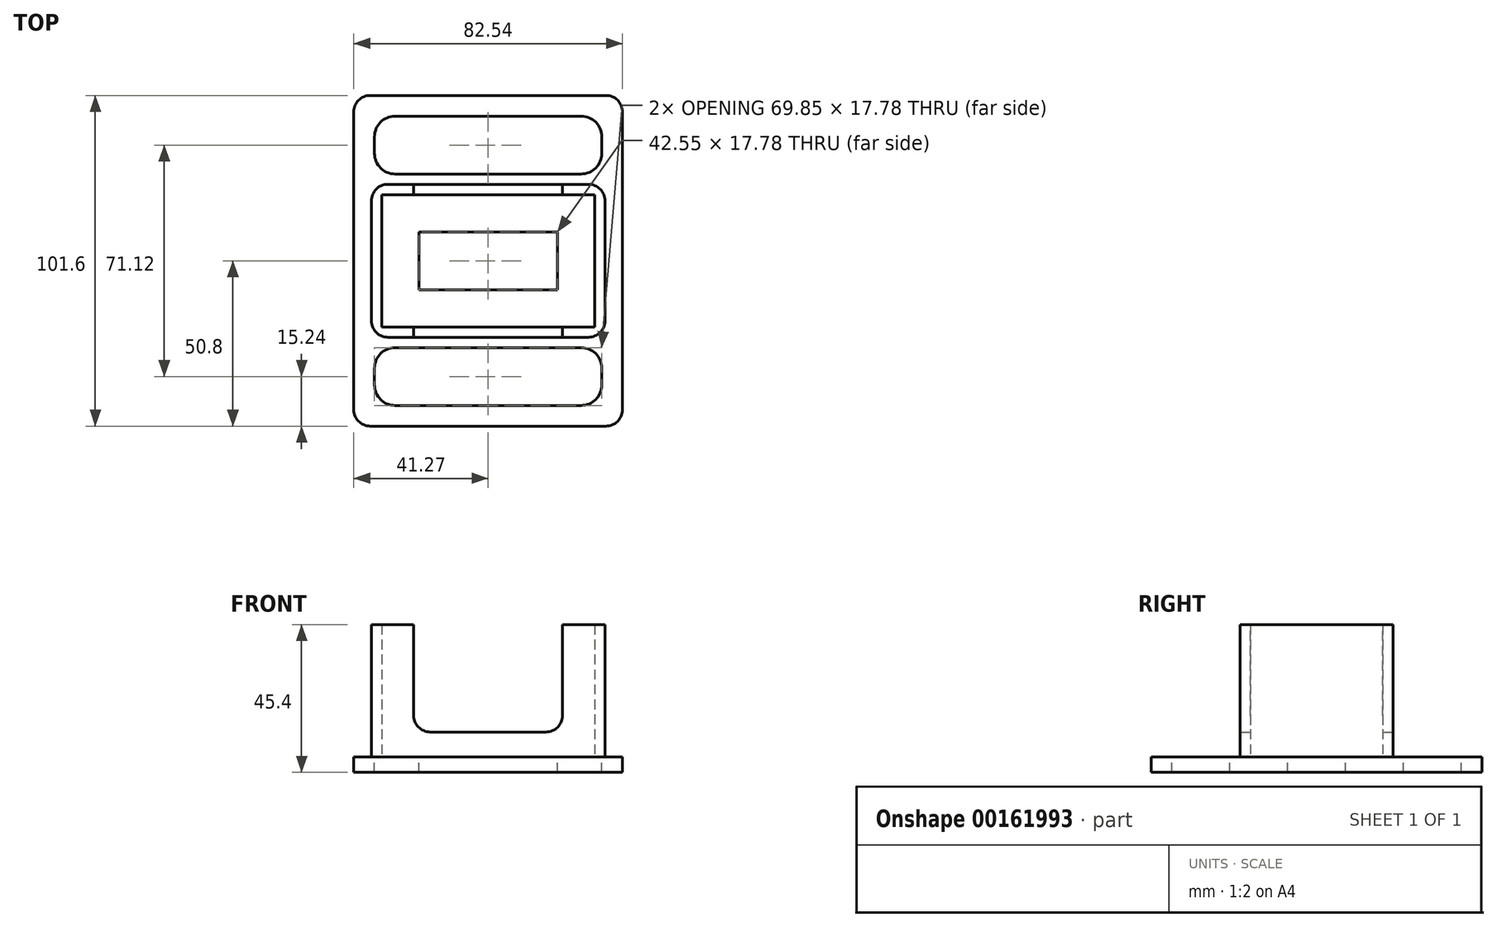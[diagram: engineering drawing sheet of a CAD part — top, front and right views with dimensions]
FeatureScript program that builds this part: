
annotation { "Feature Type Name" : "Feature", "Feature Type Description" : "" }
export const myFeature = defineFeature(function(context is Context, id is Id, definition is map)
    precondition{}
    {
        {
            var Q0;
            Q0=qCreatedBy(makeId("Top.planeOp"),FACE);
            var sketch = newSketch(context, id + "F0", { "sketchPlane" : qUnion([Q0])});
            skLineSegment(sketch, "E0.bottom", {"start": v(-41.27, 50.8) * mm, "end": v(41.28, 50.8) * mm});
            skLineSegment(sketch, "E0.top", {"start": v(-41.28, -50.8) * mm, "end": v(41.28, -50.8) * mm});
            skLineSegment(sketch, "E0.left", {"start": v(-41.27, 50.8) * mm, "end": v(-41.28, -50.8) * mm});
            skLineSegment(sketch, "E0.right", {"start": v(41.28, 50.8) * mm, "end": v(41.28, -50.8) * mm});
            skLineSegment(sketch, "E1", {"start": v(41.28, -50.8) * mm, "end": v(-41.27, 50.8) * mm, "construction": true});
            skSolve(sketch);
        }
        {
            var Q0;
            Q0 = qSketchRegion(id + "F0", true);
            extrude(context, id + "F1", {"entities" : qUnion([Q0]), "depth" : 4.76 * mm});
        }
        {
            var Q0;
            Q0=makeQuery(id+"F1.opExtrude","CAP_FACE",FACE,{"disambiguationData":[OSD([sQuery(id+"F0.wireOp",EDGE,"E0.bottom"),sQuery(id+"F0.wireOp",EDGE,"E0.top"),sQuery(id+"F0.wireOp",EDGE,"E0.left"),sQuery(id+"F0.wireOp",EDGE,"E0.right")])],"isStart":false});
            var sketch = newSketch(context, id + "F2", { "sketchPlane" : qUnion([Q0])});
            skLineSegment(sketch, "E2.bottom", {"start": v(-32.7, 20.32) * mm, "end": v(32.7, 20.32) * mm});
            skLineSegment(sketch, "E2.top", {"start": v(-32.7, -20.32) * mm, "end": v(32.7, -20.32) * mm});
            skLineSegment(sketch, "E2.left", {"start": v(-32.7, 20.32) * mm, "end": v(-32.7, -20.32) * mm});
            skLineSegment(sketch, "E2.right", {"start": v(32.7, 20.32) * mm, "end": v(32.7, -20.32) * mm});
            skPoint(sketch, "E2.middle", {"position": v(0, 0) * mm});
            skLineSegment(sketch, "E3.0", {"start": v(-35.88, 23.5) * mm, "end": v(35.88, 23.5) * mm});
            skLineSegment(sketch, "E3.1", {"start": v(-35.88, 23.5) * mm, "end": v(-35.88, -23.5) * mm});
            skLineSegment(sketch, "E3.2", {"start": v(-35.88, -23.5) * mm, "end": v(35.88, -23.5) * mm});
            skLineSegment(sketch, "E3.3", {"start": v(35.88, 23.5) * mm, "end": v(35.88, -23.5) * mm});
            skSolve(sketch);
        }
        {
            var Q0;
            Q0 = qSketchRegion(id + "F2", true);
            extrude(context, id + "F3", {"entities" : qUnion([Q0]), "operationType" : NewBodyOperationType.ADD, "depth" : 40.64 * mm});
        }
        {
            var Q0;
            Q0=qCreatedBy(makeId("Front.planeOp"),FACE);
            var sketch = newSketch(context, id + "F4", { "sketchPlane" : qUnion([Q0])});
            skLineSegment(sketch, "E4.bottom", {"start": v(22.86, 12.42) * mm, "end": v(-22.86, 12.42) * mm});
            skLineSegment(sketch, "E4.top", {"start": v(22.86, 45.4) * mm, "end": v(-22.86, 45.4) * mm});
            skLineSegment(sketch, "E4.left", {"start": v(22.86, 12.42) * mm, "end": v(22.86, 45.4) * mm});
            skLineSegment(sketch, "E4.right", {"start": v(-22.86, 12.42) * mm, "end": v(-22.86, 45.4) * mm});
            skPoint(sketch, "E4.middle", {"position": v(0, 28.91) * mm});
            skSolve(sketch);
        }
        {
            var Q0;
            Q0 = qSketchRegion(id + "F4", true);
            extrude(context, id + "F5", {"entities" : qUnion([Q0]), "operationType" : NewBodyOperationType.REMOVE, "endBound" : BoundingType.SYMMETRIC, "depth" : 80.26 * mm});
        }
        {
            var Q0;
            Q0=makeQuery(id+"F5.boolean.opBoolean","COPY",EDGE,{"derivedFrom":makeQuery(id+"F5.opExtrude","SWEPT_EDGE",EDGE,{"disambiguationData":[OSD([sQuery(id+"F4.wireOp",EDGE,"E4.bottom"),sQuery(id+"F4.wireOp",EDGE,"E4.right")])]})});
            var Q1;
            Q1=makeQuery(id+"F5.boolean.opBoolean","COPY",EDGE,{"derivedFrom":makeQuery(id+"F5.opExtrude","SWEPT_EDGE",EDGE,{"disambiguationData":[OSD([sQuery(id+"F4.wireOp",EDGE,"E4.bottom"),sQuery(id+"F4.wireOp",EDGE,"E4.left")])]})});
            fillet(context, id + "F6", {"entities" : qUnion([Q0, Q1]), "radius" : 5.08 * mm, "tangentPropagation" : true, "allowEdgeOverflow" : false});
        }
        {
            var Q0;
            Q0=makeQuery(id+"F3.opExtrude","SWEPT_EDGE",EDGE,{"disambiguationData":[OSD([sQuery(id+"F2.wireOp",EDGE,"E3.1"),sQuery(id+"F2.wireOp",EDGE,"E3.2")])]});
            var Q1;
            Q1=makeQuery(id+"F3.opExtrude","SWEPT_EDGE",EDGE,{"disambiguationData":[OSD([sQuery(id+"F2.wireOp",EDGE,"E3.0"),sQuery(id+"F2.wireOp",EDGE,"E3.1")])]});
            var Q2;
            Q2=makeQuery(id+"F3.opExtrude","SWEPT_EDGE",EDGE,{"disambiguationData":[OSD([sQuery(id+"F2.wireOp",EDGE,"E3.2"),sQuery(id+"F2.wireOp",EDGE,"E3.3")])]});
            var Q3;
            Q3=makeQuery(id+"F3.opExtrude","SWEPT_EDGE",EDGE,{"disambiguationData":[OSD([sQuery(id+"F2.wireOp",EDGE,"E3.0"),sQuery(id+"F2.wireOp",EDGE,"E3.3")])]});
            var Q4;
            Q4=makeQuery(id+"F1.opExtrude","SWEPT_EDGE",EDGE,{"disambiguationData":[OSD([sQuery(id+"F0.wireOp",EDGE,"E0.top"),sQuery(id+"F0.wireOp",EDGE,"E0.left")])]});
            var Q5;
            Q5=makeQuery(id+"F1.opExtrude","SWEPT_EDGE",EDGE,{"disambiguationData":[OSD([sQuery(id+"F0.wireOp",EDGE,"E0.top"),sQuery(id+"F0.wireOp",EDGE,"E0.right")])]});
            var Q6;
            Q6=makeQuery(id+"F1.opExtrude","SWEPT_EDGE",EDGE,{"disambiguationData":[OSD([sQuery(id+"F0.wireOp",EDGE,"E0.bottom"),sQuery(id+"F0.wireOp",EDGE,"E0.right")])]});
            var Q7;
            Q7=makeQuery(id+"F1.opExtrude","SWEPT_EDGE",EDGE,{"disambiguationData":[OSD([sQuery(id+"F0.wireOp",EDGE,"E0.bottom"),sQuery(id+"F0.wireOp",EDGE,"E0.left")])]});
            fillet(context, id + "F7", {"entities" : qUnion([Q0, Q1, Q2, Q3, Q4, Q5, Q6, Q7]), "radius" : 5.08 * mm, "tangentPropagation" : true, "allowEdgeOverflow" : false});
        }
        {
            var Q0;
            {var subQ0=sQuery(id+"F0.wireOp",EDGE,"E0.right");var subQ1=sQuery(id+"F0.wireOp",EDGE,"E0.left");var subQ2=sQuery(id+"F0.wireOp",EDGE,"E0.top");var subQ3=sQuery(id+"F0.wireOp",EDGE,"E0.bottom");Q0=makeQuery(id+"F3.boolean.opBoolean","SPLIT",FACE,{"disambiguationData":[TD([makeQuery(id+"F1.opExtrude","SWEPT_FACE",FACE,{"disambiguationData":[OSD([subQ3])]})])],"derivedFrom":makeQuery(id+"F1.opExtrude","CAP_FACE",FACE,{"disambiguationData":[OSD([subQ3,subQ2,subQ1,subQ0])],"isStart":false})});}
            var sketch = newSketch(context, id + "F8", { "sketchPlane" : qUnion([Q0])});
            skLineSegment(sketch, "E5.bottom", {"start": v(-28.57, 44.45) * mm, "end": v(28.57, 44.45) * mm});
            skLineSegment(sketch, "E5.top", {"start": v(-28.57, 26.67) * mm, "end": v(28.57, 26.67) * mm});
            skLineSegment(sketch, "E5.left", {"start": v(-34.92, 38.1) * mm, "end": v(-34.92, 33.02) * mm});
            skLineSegment(sketch, "E5.right", {"start": v(34.92, 38.1) * mm, "end": v(34.92, 33.02) * mm});
            skPoint(sketch, "E5.middle", {"position": v(0, 35.56) * mm});
            skLineSegment(sketch, "E6", {"start": v(0, 0) * mm, "end": v(-94.1, 0) * mm, "construction": true});
            skLineSegment(sketch, "E7.MirrorCS", {"start": v(-28.57, -26.67) * mm, "end": v(28.57, -26.67) * mm});
            skLineSegment(sketch, "E8.MirrorCS", {"start": v(-34.92, -38.1) * mm, "end": v(-34.92, -33.02) * mm});
            skLineSegment(sketch, "E9.MirrorCS", {"start": v(-28.57, -44.45) * mm, "end": v(28.57, -44.45) * mm});
            skLineSegment(sketch, "E10.MirrorCS", {"start": v(34.92, -38.1) * mm, "end": v(34.92, -33.02) * mm});
            skPoint(sketch, "E11.visualSharp", {"position": v(-34.92, 44.45) * mm});
            skArc(sketch, "E11.filletArc", {"start": v(-28.57, 44.45) * mm, "mid": v(-33.07, 42.6) * mm, "end": v(-34.92, 38.1) * mm});
            skPoint(sketch, "E12.visualSharp", {"position": v(-34.92, 26.67) * mm});
            skArc(sketch, "E12.filletArc", {"start": v(-34.92, 33.02) * mm, "mid": v(-33.07, 28.53) * mm, "end": v(-28.57, 26.67) * mm});
            skPoint(sketch, "E13.visualSharp", {"position": v(34.92, 44.45) * mm});
            skArc(sketch, "E13.filletArc", {"start": v(34.92, 38.1) * mm, "mid": v(33.07, 42.6) * mm, "end": v(28.57, 44.45) * mm});
            skPoint(sketch, "E14.visualSharp", {"position": v(34.92, 26.67) * mm});
            skArc(sketch, "E14.filletArc", {"start": v(28.57, 26.67) * mm, "mid": v(33.07, 28.53) * mm, "end": v(34.92, 33.02) * mm});
            skPoint(sketch, "E15.visualSharp", {"position": v(34.92, -26.67) * mm});
            skArc(sketch, "E15.filletArc", {"start": v(34.92, -33.02) * mm, "mid": v(33.07, -28.53) * mm, "end": v(28.57, -26.67) * mm});
            skPoint(sketch, "E16.visualSharp", {"position": v(34.92, -44.45) * mm});
            skArc(sketch, "E16.filletArc", {"start": v(28.57, -44.45) * mm, "mid": v(33.07, -42.6) * mm, "end": v(34.92, -38.1) * mm});
            skPoint(sketch, "E17.visualSharp", {"position": v(-34.92, -44.45) * mm});
            skArc(sketch, "E17.filletArc", {"start": v(-34.92, -38.1) * mm, "mid": v(-33.07, -42.6) * mm, "end": v(-28.57, -44.45) * mm});
            skPoint(sketch, "E18.visualSharp", {"position": v(-34.92, -26.67) * mm});
            skArc(sketch, "E18.filletArc", {"start": v(-28.57, -26.67) * mm, "mid": v(-33.07, -28.53) * mm, "end": v(-34.92, -33.02) * mm});
            skSolve(sketch);
        }
        {
            var Q0;
            Q0 = qSketchRegion(id + "F8", true);
            extrude(context, id + "F9", {"entities" : qUnion([Q0]), "operationType" : NewBodyOperationType.REMOVE, "oppositeDirection" : true, "depth" : 25.4 * mm});
        }
        {
            var Q0;
            Q0=makeQuery(id+"F3.boolean.opBoolean","SPLIT",FACE,{"disambiguationData":[TD([makeQuery(id+"F3.opExtrude","SWEPT_FACE",FACE,{"disambiguationData":[OSD([sQuery(id+"F2.wireOp",EDGE,"E2.bottom")])]})])],"derivedFrom":makeQuery(id+"F1.opExtrude","CAP_FACE",FACE,{"disambiguationData":[OSD([sQuery(id+"F0.wireOp",EDGE,"E0.bottom"),sQuery(id+"F0.wireOp",EDGE,"E0.top"),sQuery(id+"F0.wireOp",EDGE,"E0.left"),sQuery(id+"F0.wireOp",EDGE,"E0.right")])],"isStart":false})});
            var sketch = newSketch(context, id + "F10", { "sketchPlane" : qUnion([Q0])});
            skLineSegment(sketch, "E19.0", {"start": v(21.27, 8.9) * mm, "end": v(-21.27, 8.9) * mm});
            skLineSegment(sketch, "E19.1", {"start": v(21.27, -8.9) * mm, "end": v(21.27, 8.9) * mm});
            skLineSegment(sketch, "E19.2", {"start": v(-21.27, -8.9) * mm, "end": v(21.27, -8.9) * mm});
            skLineSegment(sketch, "E19.3", {"start": v(-21.27, 8.9) * mm, "end": v(-21.27, -8.9) * mm});
            skSolve(sketch);
        }
        {
            var Q0;
            Q0 = qSketchRegion(id + "F10", true);
            extrude(context, id + "F11", {"entities" : qUnion([Q0]), "operationType" : NewBodyOperationType.REMOVE, "oppositeDirection" : true, "depth" : 25.4 * mm});
        }
    });
